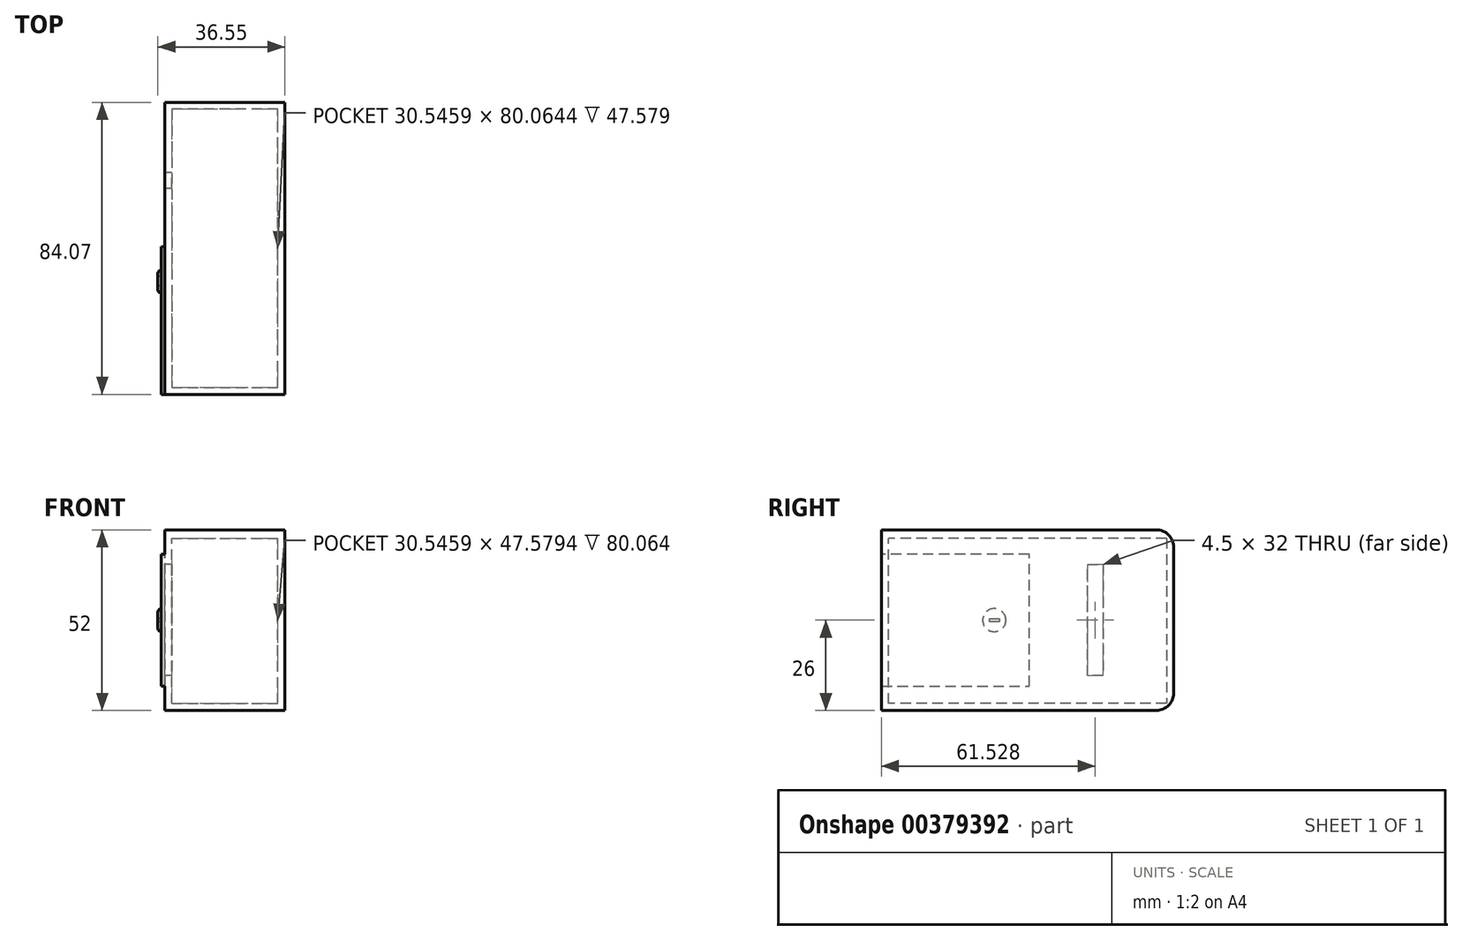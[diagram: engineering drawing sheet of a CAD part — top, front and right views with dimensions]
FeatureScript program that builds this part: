
annotation { "Feature Type Name" : "Feature", "Feature Type Description" : "" }
export const myFeature = defineFeature(function(context is Context, id is Id, definition is map)
    precondition{}
    {
        {
            var Q0;
            Q0=qCreatedBy(makeId("Top.planeOp"),FACE);
            var sketch = newSketch(context, id + "F0", { "sketchPlane" : qUnion([Q0])});
            skLineSegment(sketch, "E0", {"start": v(-48.8, 41.55) * mm, "end": v(-48.8, -42.52) * mm});
            skLineSegment(sketch, "E1", {"start": v(-48.8, -42.52) * mm, "end": v(-14.25, -42.52) * mm});
            skLineSegment(sketch, "E2", {"start": v(-14.25, -42.52) * mm, "end": v(-14.25, 41.55) * mm});
            skLineSegment(sketch, "E3", {"start": v(-14.25, 41.55) * mm, "end": v(-48.8, 41.55) * mm});
            skSolve(sketch);
        }
        {
            var Q0;
            Q0=makeQuery(id+"F0.imprint","IMPRINT",FACE,{"disambiguationData":[TD([[makeQuery(id+"F0.imprint","IMPRINT",EDGE,{"derivedFrom":sQuery(id+"F0.wireOp",EDGE,"E0")}),1.0]])]});
            extrude(context, id + "F1", {"entities" : qUnion([Q0]), "depth" : 2 * mm});
        }
        {
            var Q0;
            Q0=makeQuery(id+"F1.opExtrude","CAP_FACE",FACE,{"disambiguationData":[OSD([sQuery(id+"F0.wireOp",EDGE,"E0"),sQuery(id+"F0.wireOp",EDGE,"E1"),sQuery(id+"F0.wireOp",EDGE,"E2"),sQuery(id+"F0.wireOp",EDGE,"E3")])],"isStart":false});
            var sketch = newSketch(context, id + "F2", { "sketchPlane" : qUnion([Q0])});
            skLineSegment(sketch, "E4", {"start": v(-14.25, 41.55) * mm, "end": v(-16.25, 41.55) * mm});
            skLineSegment(sketch, "E5", {"start": v(-16.25, 41.55) * mm, "end": v(-16.25, -42.52) * mm});
            skLineSegment(sketch, "E6", {"start": v(-16.25, -42.52) * mm, "end": v(-14.25, -42.52) * mm});
            skLineSegment(sketch, "E7", {"start": v(-14.25, -42.52) * mm, "end": v(-14.25, 41.55) * mm});
            skPoint(sketch, "E8.start.orphan", {"position": v(-46.8, -42.52) * mm});
            skSolve(sketch);
        }
        {
            var Q0;
            Q0=makeQuery(id+"F2.imprint","IMPRINT",FACE,{"disambiguationData":[TD([[makeQuery(id+"F2.imprint","IMPRINT",EDGE,{"derivedFrom":sQuery(id+"F2.wireOp",EDGE,"E4")}),1.0]])]});
            extrude(context, id + "F3", {"entities" : qUnion([Q0]), "operationType" : NewBodyOperationType.ADD, "depth" : 50 * mm});
        }
        {
            var Q0;
            Q0=makeQuery(id+"F1.opExtrude","CAP_FACE",FACE,{"disambiguationData":[OSD([sQuery(id+"F0.wireOp",EDGE,"E0"),sQuery(id+"F0.wireOp",EDGE,"E1"),sQuery(id+"F0.wireOp",EDGE,"E2"),sQuery(id+"F0.wireOp",EDGE,"E3")])],"isStart":false});
            var sketch = newSketch(context, id + "F4", { "sketchPlane" : qUnion([Q0])});
            skLineSegment(sketch, "E9", {"start": v(-48.8, 41.55) * mm, "end": v(-46.8, 41.55) * mm});
            skLineSegment(sketch, "E10", {"start": v(-46.8, 41.55) * mm, "end": v(-46.8, -42.52) * mm});
            skLineSegment(sketch, "E11", {"start": v(-46.8, -42.52) * mm, "end": v(-48.8, -42.52) * mm});
            skLineSegment(sketch, "E12", {"start": v(-48.8, -42.52) * mm, "end": v(-48.8, 41.55) * mm});
            skSolve(sketch);
        }
        {
            var Q0;
            Q0=makeQuery(id+"F4.imprint","IMPRINT",FACE,{"disambiguationData":[TD([[makeQuery(id+"F4.imprint","IMPRINT",EDGE,{"derivedFrom":sQuery(id+"F4.wireOp",EDGE,"E9")}),1.0]])]});
            extrude(context, id + "F5", {"entities" : qUnion([Q0]), "operationType" : NewBodyOperationType.ADD, "depth" : 50 * mm});
        }
        {
            var Q0;
            Q0=makeQuery(id+"F5.opExtrude","SWEPT_FACE",FACE,{"disambiguationData":[OSD([sQuery(id+"F4.wireOp",EDGE,"E10")])]});
            var sketch = newSketch(context, id + "F6", { "sketchPlane" : qUnion([Q0])});
            skLineSegment(sketch, "E13", {"start": v(41.55, 52) * mm, "end": v(41.55, 49.58) * mm});
            skLineSegment(sketch, "E14", {"start": v(41.55, 49.58) * mm, "end": v(-42.52, 49.58) * mm});
            skLineSegment(sketch, "E15", {"start": v(-42.52, 49.58) * mm, "end": v(-42.52, 52) * mm});
            skLineSegment(sketch, "E16", {"start": v(-42.52, 52) * mm, "end": v(41.55, 52) * mm});
            skSolve(sketch);
        }
        {
            var Q0;
            Q0=makeQuery(id+"F6.imprint","IMPRINT",FACE,{"disambiguationData":[TD([[makeQuery(id+"F6.imprint","IMPRINT",EDGE,{"derivedFrom":sQuery(id+"F6.wireOp",EDGE,"E13")}),-1.0]])]});
            extrude(context, id + "F7", {"entities" : qUnion([Q0]), "operationType" : NewBodyOperationType.ADD, "depth" : 32.2 * mm});
        }
        {
            var Q0;
            Q0=makeQuery(id+"F1.opExtrude","CAP_FACE",FACE,{"disambiguationData":[OSD([sQuery(id+"F0.wireOp",EDGE,"E0"),sQuery(id+"F0.wireOp",EDGE,"E1"),sQuery(id+"F0.wireOp",EDGE,"E2"),sQuery(id+"F0.wireOp",EDGE,"E3")])],"isStart":false});
            var sketch = newSketch(context, id + "F8", { "sketchPlane" : qUnion([Q0])});
            skLineSegment(sketch, "E17", {"start": v(-46.8, 41.55) * mm, "end": v(-16.25, 41.55) * mm});
            skLineSegment(sketch, "E18", {"start": v(-16.25, 41.55) * mm, "end": v(-16.25, 39.55) * mm});
            skLineSegment(sketch, "E19", {"start": v(-16.25, 39.55) * mm, "end": v(-46.8, 39.55) * mm});
            skLineSegment(sketch, "E20", {"start": v(-46.8, 39.55) * mm, "end": v(-46.8, 41.55) * mm});
            skSolve(sketch);
        }
        {
            var Q0;
            Q0=makeQuery(id+"F8.imprint","IMPRINT",FACE,{"disambiguationData":[TD([[makeQuery(id+"F8.imprint","IMPRINT",EDGE,{"derivedFrom":sQuery(id+"F8.wireOp",EDGE,"E17")}),1.0]])]});
            extrude(context, id + "F9", {"entities" : qUnion([Q0]), "operationType" : NewBodyOperationType.ADD, "depth" : 47.6 * mm});
        }
        {
            var Q0;
            Q0=makeQuery(id+"F7.boolean.opBoolean","MERGE",EDGE,{"derivedFrom":[makeQuery(id+"F3.opExtrude","CAP_EDGE",EDGE,{"disambiguationData":[OSD([sQuery(id+"F2.wireOp",EDGE,"E4")])],"isStart":false}),makeQuery(id+"F5.opExtrude","CAP_EDGE",EDGE,{"disambiguationData":[OSD([sQuery(id+"F4.wireOp",EDGE,"E9")])],"isStart":false}),makeQuery(id+"F7.opExtrude","SWEPT_EDGE",EDGE,{"disambiguationData":[OSD([sQuery(id+"F6.wireOp",EDGE,"E13"),sQuery(id+"F6.wireOp",EDGE,"E16")])]})]});
            fillet(context, id + "F10", {"entities" : qUnion([Q0]), "radius" : 5 * mm, "tangentPropagation" : true, "allowEdgeOverflow" : false});
        }
        {
            var Q0;
            Q0=makeQuery(id+"F1.opExtrude","CAP_EDGE",EDGE,{"disambiguationData":[OSD([sQuery(id+"F0.wireOp",EDGE,"E3")])],"isStart":true});
            fillet(context, id + "F11", {"entities" : qUnion([Q0]), "radius" : 5 * mm, "tangentPropagation" : true, "allowEdgeOverflow" : false});
        }
        {
            var Q0;
            Q0=makeQuery(id+"F3.opExtrude","SWEPT_FACE",FACE,{"disambiguationData":[OSD([sQuery(id+"F2.wireOp",EDGE,"E5")])]});
            var sketch = newSketch(context, id + "F12", { "sketchPlane" : qUnion([Q0])});
            skLineSegment(sketch, "E21", {"start": v(42.52, 49.58) * mm, "end": v(42.52, 2) * mm});
            skLineSegment(sketch, "E22", {"start": v(42.52, 2) * mm, "end": v(40.52, 2) * mm});
            skLineSegment(sketch, "E23", {"start": v(40.52, 2) * mm, "end": v(40.52, 49.58) * mm});
            skLineSegment(sketch, "E24", {"start": v(40.52, 49.58) * mm, "end": v(42.52, 49.58) * mm});
            skSolve(sketch);
        }
        {
            var Q0;
            Q0=makeQuery(id+"F12.imprint","IMPRINT",FACE,{"disambiguationData":[TD([[makeQuery(id+"F12.imprint","IMPRINT",EDGE,{"derivedFrom":sQuery(id+"F12.wireOp",EDGE,"E21")}),-1.0]])]});
            extrude(context, id + "F13", {"entities" : qUnion([Q0]), "operationType" : NewBodyOperationType.ADD, "depth" : 31.3 * mm});
        }
        {
            var Q0;
            Q0=makeQuery(id+"F5.boolean.opBoolean","MERGE",FACE,{"derivedFrom":[makeQuery(id+"F1.opExtrude","SWEPT_FACE",FACE,{"disambiguationData":[OSD([sQuery(id+"F0.wireOp",EDGE,"E0")])]}),makeQuery(id+"F5.opExtrude","SWEPT_FACE",FACE,{"disambiguationData":[OSD([sQuery(id+"F4.wireOp",EDGE,"E12")])]})]});
            var sketch = newSketch(context, id + "F14", { "sketchPlane" : qUnion([Q0])});
            skPoint(sketch, "E25.startSnap0", {"position": v(-41.55, 26) * mm});
            skLineSegment(sketch, "E26", {"start": v(-21.26, 10) * mm, "end": v(-21.26, 42) * mm});
            skLineSegment(sketch, "E27", {"start": v(-21.26, 42) * mm, "end": v(-16.76, 42) * mm});
            skLineSegment(sketch, "E28", {"start": v(-16.76, 42) * mm, "end": v(-16.76, 10) * mm});
            skLineSegment(sketch, "E29", {"start": v(-16.76, 10) * mm, "end": v(-21.26, 10) * mm});
            skPoint(sketch, "E30.start.orphan", {"position": v(-21.26, 52) * mm});
            skSolve(sketch);
        }
        {
            var Q0;
            Q0=makeQuery(id+"F14.imprint","IMPRINT",FACE,{"disambiguationData":[TD([[makeQuery(id+"F14.imprint","IMPRINT",EDGE,{"derivedFrom":sQuery(id+"F14.wireOp",EDGE,"E26")}),-1.0]])]});
            extrude(context, id + "F15", {"entities" : qUnion([Q0]), "operationType" : NewBodyOperationType.REMOVE, "oppositeDirection" : true, "depth" : 25 * mm});
        }
        {
            var Q0;
            Q0=makeQuery(id+"F5.boolean.opBoolean","MERGE",FACE,{"derivedFrom":[makeQuery(id+"F1.opExtrude","SWEPT_FACE",FACE,{"disambiguationData":[OSD([sQuery(id+"F0.wireOp",EDGE,"E0")])]}),makeQuery(id+"F5.opExtrude","SWEPT_FACE",FACE,{"disambiguationData":[OSD([sQuery(id+"F4.wireOp",EDGE,"E12")])]})]});
            var sketch = newSketch(context, id + "F16", { "sketchPlane" : qUnion([Q0])});
            skLineSegment(sketch, "E31", {"start": v(42.52, 7) * mm, "end": v(0, 7) * mm});
            skLineSegment(sketch, "E32", {"start": v(0, 7) * mm, "end": v(0, 45) * mm});
            skLineSegment(sketch, "E33", {"start": v(0, 45) * mm, "end": v(42.52, 45) * mm});
            skLineSegment(sketch, "E34", {"start": v(42.52, 45) * mm, "end": v(42.52, 7) * mm});
            skSolve(sketch);
        }
        {
            var Q0;
            Q0=makeQuery(id+"F16.imprint","IMPRINT",FACE,{"disambiguationData":[TD([[makeQuery(id+"F16.imprint","IMPRINT",EDGE,{"derivedFrom":sQuery(id+"F16.wireOp",EDGE,"E31")}),-1.0]])]});
            extrude(context, id + "F17", {"entities" : qUnion([Q0]), "operationType" : NewBodyOperationType.ADD, "depth" : 1 * mm});
        }
        {
            var Q0;
            Q0=makeQuery(id+"F17.opExtrude","CAP_FACE",FACE,{"disambiguationData":[OSD([sQuery(id+"F16.wireOp",EDGE,"E31"),sQuery(id+"F16.wireOp",EDGE,"E32"),sQuery(id+"F16.wireOp",EDGE,"E33"),sQuery(id+"F16.wireOp",EDGE,"E34")])],"isStart":false});
            var sketch = newSketch(context, id + "F18", { "sketchPlane" : qUnion([Q0])});
            skCircle(sketch, "E35", {"center": v(10.06, 26) * mm, "radius": 3.33 * mm});
            skPoint(sketch, "E35.centerSnap0", {"position": v(0, 26) * mm});
            skSolve(sketch);
        }
        {
            var Q0;
            Q0=makeQuery(id+"F18.imprint","IMPRINT",FACE,{"disambiguationData":[TD([[makeQuery(id+"F18.imprint","IMPRINT",EDGE,{"derivedFrom":sQuery(id+"F18.wireOp",EDGE,"E35")}),1.0]])]});
            extrude(context, id + "F19", {"entities" : qUnion([Q0]), "operationType" : NewBodyOperationType.ADD, "depth" : 1 * mm});
        }
        {
            var Q0;
            Q0=makeQuery(id+"F19.opExtrude","CAP_EDGE",EDGE,{"disambiguationData":[OSD([sQuery(id+"F18.wireOp",EDGE,"E35")])],"isStart":false});
            fillet(context, id + "F20", {"entities" : qUnion([Q0]), "radius" : 1 * mm, "tangentPropagation" : true, "allowEdgeOverflow" : false});
        }
        {
            var Q0;
            Q0=makeQuery(id+"F19.opExtrude","CAP_FACE",FACE,{"disambiguationData":[OSD([sQuery(id+"F18.wireOp",EDGE,"E35")])],"isStart":false});
            var sketch = newSketch(context, id + "F21", { "sketchPlane" : qUnion([Q0])});
            skPoint(sketch, "E36.start.orphan", {"position": v(10.06, 26) * mm});
            skLineSegment(sketch, "E37", {"start": v(10.06, 26.43) * mm, "end": v(8.55, 26.43) * mm});
            skLineSegment(sketch, "E38", {"start": v(8.55, 26.43) * mm, "end": v(8.55, 25.57) * mm});
            skLineSegment(sketch, "E39", {"start": v(8.55, 25.57) * mm, "end": v(11.38, 25.57) * mm});
            skLineSegment(sketch, "E40", {"start": v(11.38, 25.57) * mm, "end": v(11.38, 26.43) * mm});
            skLineSegment(sketch, "E41", {"start": v(11.38, 26.43) * mm, "end": v(10.06, 26.43) * mm});
            skPoint(sketch, "E42.start.orphan", {"position": v(10.06, 28.33) * mm});
            skPoint(sketch, "E43.end.orphan", {"position": v(10.06, 25.57) * mm});
            skPoint(sketch, "E43.start.orphan", {"position": v(10.06, 23.67) * mm});
            skSolve(sketch);
        }
        {
            var Q0;
            Q0=makeQuery(id+"F21.imprint","IMPRINT",FACE,{"disambiguationData":[TD([[makeQuery(id+"F21.imprint","IMPRINT",EDGE,{"derivedFrom":sQuery(id+"F21.wireOp",EDGE,"E37")}),1.0]])]});
            extrude(context, id + "F22", {"entities" : qUnion([Q0]), "operationType" : NewBodyOperationType.REMOVE, "oppositeDirection" : true, "depth" : 1 * mm});
        }
    });
